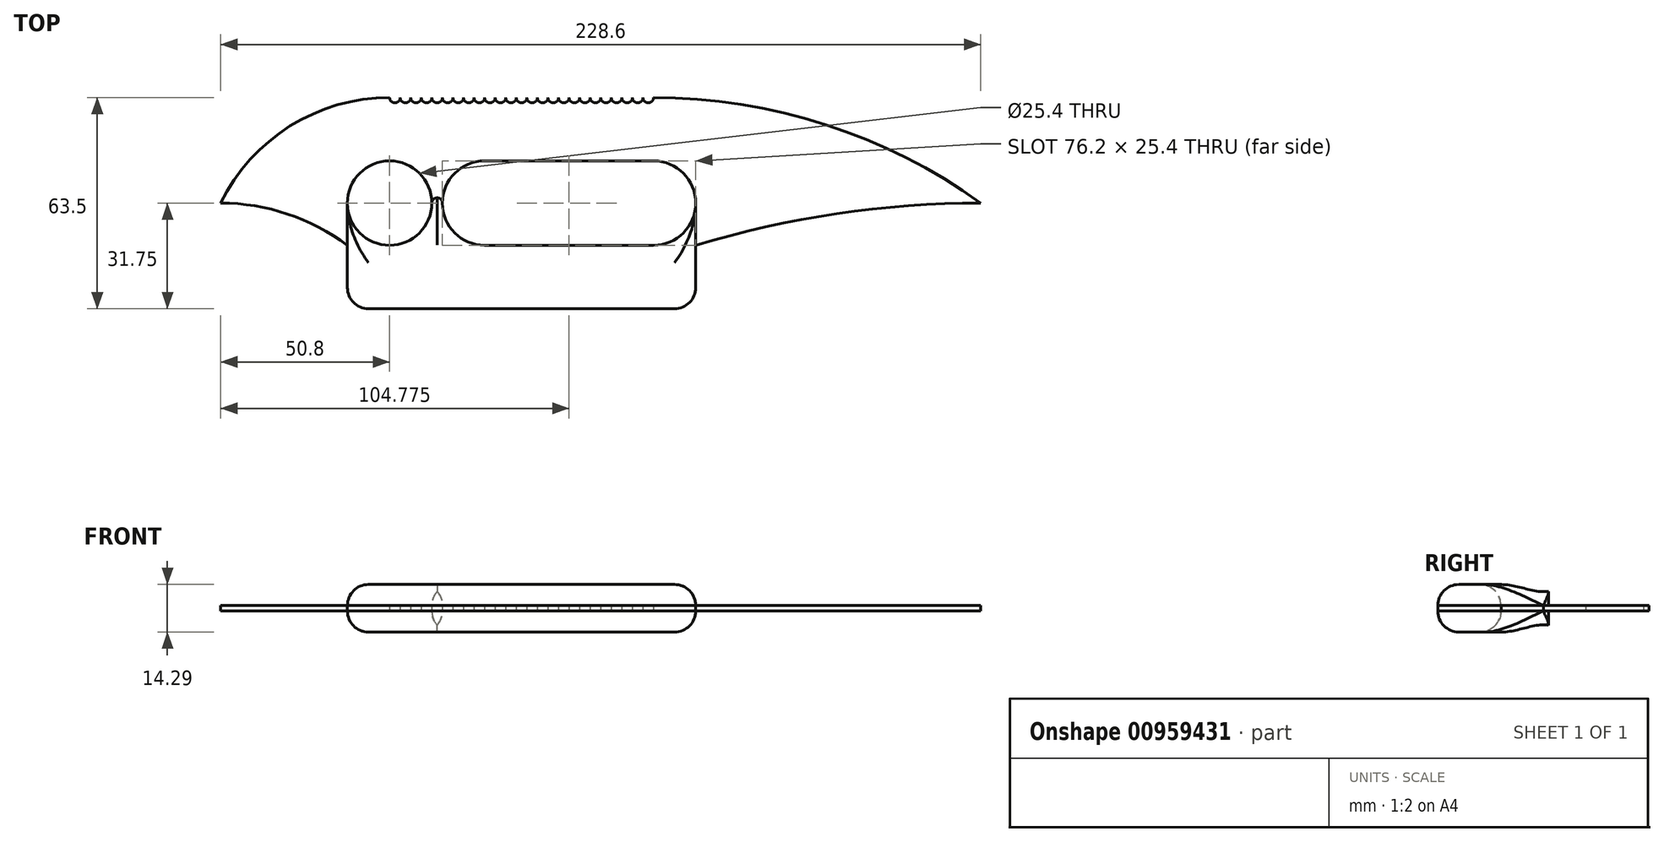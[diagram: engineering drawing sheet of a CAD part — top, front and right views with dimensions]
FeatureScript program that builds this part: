
annotation { "Feature Type Name" : "Feature", "Feature Type Description" : "" }
export const myFeature = defineFeature(function(context is Context, id is Id, definition is map)
    precondition{}
    {
        {
            var Q0;
            Q0=qCreatedBy(makeId("Top.planeOp"),FACE);
            var sketch = newSketch(context, id + "F0", { "sketchPlane" : qUnion([Q0])});
            skCircle(sketch, "E0", {"center": v(0, 0) * mm, "radius": 127 * mm, "construction": true});
            skCircle(sketch, "E1", {"center": v(-63.5, 0) * mm, "radius": 12.7 * mm});
            skArc(sketch, "E2", {"start": v(-34.92, -12.7) * mm, "mid": v(-47.62, 0) * mm, "end": v(-34.92, 12.7) * mm});
            skArc(sketch, "E3", {"start": v(15.88, 12.7) * mm, "mid": v(28.58, 0) * mm, "end": v(15.88, -12.7) * mm});
            skLineSegment(sketch, "E4", {"start": v(-34.92, 12.7) * mm, "end": v(15.88, 12.7) * mm});
            skLineSegment(sketch, "E5", {"start": v(15.88, -12.7) * mm, "end": v(-34.92, -12.7) * mm});
            skPoint(sketch, "E6", {"position": v(-114.3, 0) * mm});
            skPoint(sketch, "E7", {"position": v(114.3, 0) * mm});
            skPoint(sketch, "E8", {"position": v(-76.2, 0) * mm});
            skPoint(sketch, "E9", {"position": v(-63.5, -12.7) * mm});
            skPoint(sketch, "E10.oppositeSnap0", {"position": v(28.58, 0) * mm});
            skLineSegment(sketch, "E10.bottom", {"start": v(-76.2, -12.7) * mm, "end": v(28.58, -12.7) * mm, "construction": true});
            skLineSegment(sketch, "E10.top", {"start": v(-69.85, -31.75) * mm, "end": v(22.23, -31.75) * mm});
            skLineSegment(sketch, "E10.left", {"start": v(-76.2, -12.7) * mm, "end": v(-76.2, -25.4) * mm});
            skLineSegment(sketch, "E10.right", {"start": v(28.58, -12.7) * mm, "end": v(28.58, -25.4) * mm});
            skArc(sketch, "E11", {"start": v(-76.2, -12.7) * mm, "mid": v(-94.22, -3.26) * mm, "end": v(-114.3, 0) * mm});
            skLineSegment(sketch, "E12", {"start": v(-114.3, 0) * mm, "end": v(114.3, 0) * mm, "construction": true});
            skArc(sketch, "E13", {"start": v(114.3, 0) * mm, "mid": v(70.97, -3.2) * mm, "end": v(28.57, -12.7) * mm});
            skArc(sketch, "E14", {"start": v(114.3, 0) * mm, "mid": v(67.58, 23.62) * mm, "end": v(15.88, 31.75) * mm});
            skArc(sketch, "E15", {"start": v(-63.5, 31.75) * mm, "mid": v(-93.45, 23.16) * mm, "end": v(-114.3, 0) * mm});
            skLineSegment(sketch, "E16", {"start": v(-63.5, 31.75) * mm, "end": v(15.88, 31.75) * mm, "construction": true});
            skPoint(sketch, "E17.visualSharp", {"position": v(-76.2, -31.75) * mm});
            skArc(sketch, "E17.filletArc", {"start": v(-76.2, -25.4) * mm, "mid": v(-74.34, -29.9) * mm, "end": v(-69.85, -31.75) * mm});
            skPoint(sketch, "E18.visualSharp", {"position": v(28.58, -31.75) * mm});
            skArc(sketch, "E18.filletArc", {"start": v(22.23, -31.75) * mm, "mid": v(26.72, -29.9) * mm, "end": v(28.58, -25.4) * mm});
            skArc(sketch, "E19", {"start": v(-63.5, 31.75) * mm, "mid": v(-61.91, 30.16) * mm, "end": v(-60.32, 31.75) * mm});
            skArc(sketch, "E20", {"start": v(-60.33, 31.75) * mm, "mid": v(-58.74, 30.16) * mm, "end": v(-57.15, 31.75) * mm});
            skArc(sketch, "E21", {"start": v(-57.15, 31.75) * mm, "mid": v(-55.56, 30.16) * mm, "end": v(-53.98, 31.75) * mm});
            skArc(sketch, "E22", {"start": v(-53.98, 31.75) * mm, "mid": v(-52.39, 30.16) * mm, "end": v(-50.8, 31.75) * mm});
            skArc(sketch, "E23", {"start": v(-50.8, 31.75) * mm, "mid": v(-49.21, 30.16) * mm, "end": v(-47.63, 31.75) * mm});
            skArc(sketch, "E24", {"start": v(-47.63, 31.75) * mm, "mid": v(-46.04, 30.16) * mm, "end": v(-44.45, 31.75) * mm});
            skArc(sketch, "E25", {"start": v(-44.45, 31.75) * mm, "mid": v(-42.86, 30.16) * mm, "end": v(-41.28, 31.75) * mm});
            skArc(sketch, "E26", {"start": v(-41.28, 31.75) * mm, "mid": v(-39.69, 30.16) * mm, "end": v(-38.1, 31.75) * mm});
            skArc(sketch, "E27", {"start": v(-38.1, 31.75) * mm, "mid": v(-36.51, 30.16) * mm, "end": v(-34.93, 31.75) * mm});
            skArc(sketch, "E28", {"start": v(-34.93, 31.75) * mm, "mid": v(-33.34, 30.16) * mm, "end": v(-31.75, 31.75) * mm});
            skArc(sketch, "E29", {"start": v(-31.75, 31.75) * mm, "mid": v(-30.16, 30.16) * mm, "end": v(-28.58, 31.75) * mm});
            skArc(sketch, "E30", {"start": v(-28.58, 31.75) * mm, "mid": v(-26.99, 30.16) * mm, "end": v(-25.4, 31.75) * mm});
            skArc(sketch, "E31", {"start": v(-25.4, 31.75) * mm, "mid": v(-23.81, 30.16) * mm, "end": v(-22.23, 31.75) * mm});
            skArc(sketch, "E32", {"start": v(-22.23, 31.75) * mm, "mid": v(-20.64, 30.16) * mm, "end": v(-19.05, 31.75) * mm});
            skArc(sketch, "E33", {"start": v(-19.05, 31.75) * mm, "mid": v(-17.46, 30.16) * mm, "end": v(-15.88, 31.75) * mm});
            skArc(sketch, "E34", {"start": v(-15.88, 31.75) * mm, "mid": v(-14.29, 30.16) * mm, "end": v(-12.7, 31.75) * mm});
            skArc(sketch, "E35", {"start": v(-12.7, 31.75) * mm, "mid": v(-11.11, 30.16) * mm, "end": v(-9.53, 31.75) * mm});
            skArc(sketch, "E36", {"start": v(-9.53, 31.75) * mm, "mid": v(-7.94, 30.16) * mm, "end": v(-6.35, 31.75) * mm});
            skArc(sketch, "E37", {"start": v(-6.35, 31.75) * mm, "mid": v(-4.76, 30.16) * mm, "end": v(-3.18, 31.75) * mm});
            skArc(sketch, "E38", {"start": v(-3.18, 31.75) * mm, "mid": v(-1.59, 30.16) * mm, "end": v(0, 31.75) * mm});
            skArc(sketch, "E39", {"start": v(0, 31.75) * mm, "mid": v(1.59, 30.16) * mm, "end": v(3.17, 31.75) * mm});
            skArc(sketch, "E40", {"start": v(3.17, 31.75) * mm, "mid": v(4.76, 30.16) * mm, "end": v(6.35, 31.75) * mm});
            skArc(sketch, "E41", {"start": v(6.35, 31.75) * mm, "mid": v(7.94, 30.16) * mm, "end": v(9.52, 31.75) * mm});
            skArc(sketch, "E42", {"start": v(9.52, 31.75) * mm, "mid": v(11.11, 30.16) * mm, "end": v(12.7, 31.75) * mm});
            skArc(sketch, "E43", {"start": v(12.7, 31.75) * mm, "mid": v(14.29, 30.16) * mm, "end": v(15.87, 31.75) * mm});
            skSolve(sketch);
        }
        {
            var Q0;
            Q0 = qSketchRegion(id + "F0", true);
            extrude(context, id + "F1", {"entities" : qUnion([Q0]), "depth" : 1.59 * mm, "offsetDistance" : 25.4 * mm});
        }
        {
            var Q0;
            Q0=makeQuery(id+"F1.opExtrude","CAP_FACE",FACE,{"disambiguationData":[OSD([sQuery(id+"F0.wireOp",EDGE,"E1"),sQuery(id+"F0.wireOp",EDGE,"E2"),sQuery(id+"F0.wireOp",EDGE,"E3"),sQuery(id+"F0.wireOp",EDGE,"E4"),sQuery(id+"F0.wireOp",EDGE,"E5"),sQuery(id+"F0.wireOp",EDGE,"E10.top"),sQuery(id+"F0.wireOp",EDGE,"E10.left"),sQuery(id+"F0.wireOp",EDGE,"E10.right"),sQuery(id+"F0.wireOp",EDGE,"E11"),sQuery(id+"F0.wireOp",EDGE,"E13"),sQuery(id+"F0.wireOp",EDGE,"E14"),sQuery(id+"F0.wireOp",EDGE,"E15"),sQuery(id+"F0.wireOp",EDGE,"E17.filletArc"),sQuery(id+"F0.wireOp",EDGE,"E18.filletArc"),sQuery(id+"F0.wireOp",EDGE,"E19"),sQuery(id+"F0.wireOp",EDGE,"E20"),sQuery(id+"F0.wireOp",EDGE,"E21"),sQuery(id+"F0.wireOp",EDGE,"E22"),sQuery(id+"F0.wireOp",EDGE,"E23"),sQuery(id+"F0.wireOp",EDGE,"E24"),sQuery(id+"F0.wireOp",EDGE,"E25"),sQuery(id+"F0.wireOp",EDGE,"E26"),sQuery(id+"F0.wireOp",EDGE,"E27"),sQuery(id+"F0.wireOp",EDGE,"E28"),sQuery(id+"F0.wireOp",EDGE,"E29"),sQuery(id+"F0.wireOp",EDGE,"E30"),sQuery(id+"F0.wireOp",EDGE,"E31"),sQuery(id+"F0.wireOp",EDGE,"E32"),sQuery(id+"F0.wireOp",EDGE,"E33"),sQuery(id+"F0.wireOp",EDGE,"E34"),sQuery(id+"F0.wireOp",EDGE,"E35"),sQuery(id+"F0.wireOp",EDGE,"E36"),sQuery(id+"F0.wireOp",EDGE,"E37"),sQuery(id+"F0.wireOp",EDGE,"E38"),sQuery(id+"F0.wireOp",EDGE,"E39"),sQuery(id+"F0.wireOp",EDGE,"E40"),sQuery(id+"F0.wireOp",EDGE,"E41"),sQuery(id+"F0.wireOp",EDGE,"E42"),sQuery(id+"F0.wireOp",EDGE,"E43")])],"isStart":false});
            var sketch = newSketch(context, id + "F2", { "sketchPlane" : qUnion([Q0])});
            skLineSegment(sketch, "E44", {"start": v(-76.2, -12.7) * mm, "end": v(-76.2, 0) * mm});
            skLineSegment(sketch, "E45", {"start": v(28.58, -12.7) * mm, "end": v(28.58, 0) * mm});
            skArc(sketch, "E46", {"start": v(-47.62, 0) * mm, "mid": v(-49.21, 1.59) * mm, "end": v(-50.8, 0) * mm});
            skPoint(sketch, "E46.endSnap0", {"position": v(-47.62, 0) * mm});
            skSolve(sketch);
        }
        {
            var Q0;
            {var subQ3=sQuery(id+"F2.wireOp",EDGE,"E44");Q0=makeQuery(id+"F2.imprint","IMPRINT",FACE,{"disambiguationData":[TD([[makeQuery(id+"F2.imprint","IMPRINT",EDGE,{"derivedFrom":subQ3}),-1.0]])]});}
            extrude(context, id + "F3", {"entities" : qUnion([Q0]), "depth" : 6.35 * mm, "offsetDistance" : 25.4 * mm});
        }
        {
            var Q0;
            Q0=makeQuery(id+"F1.opExtrude","CAP_FACE",FACE,{"disambiguationData":[OSD([sQuery(id+"F0.wireOp",EDGE,"E1"),sQuery(id+"F0.wireOp",EDGE,"E2"),sQuery(id+"F0.wireOp",EDGE,"E3"),sQuery(id+"F0.wireOp",EDGE,"E4"),sQuery(id+"F0.wireOp",EDGE,"E5"),sQuery(id+"F0.wireOp",EDGE,"E10.top"),sQuery(id+"F0.wireOp",EDGE,"E10.left"),sQuery(id+"F0.wireOp",EDGE,"E10.right"),sQuery(id+"F0.wireOp",EDGE,"E11"),sQuery(id+"F0.wireOp",EDGE,"E13"),sQuery(id+"F0.wireOp",EDGE,"E14"),sQuery(id+"F0.wireOp",EDGE,"E15"),sQuery(id+"F0.wireOp",EDGE,"E17.filletArc"),sQuery(id+"F0.wireOp",EDGE,"E18.filletArc"),sQuery(id+"F0.wireOp",EDGE,"E19"),sQuery(id+"F0.wireOp",EDGE,"E20"),sQuery(id+"F0.wireOp",EDGE,"E21"),sQuery(id+"F0.wireOp",EDGE,"E22"),sQuery(id+"F0.wireOp",EDGE,"E23"),sQuery(id+"F0.wireOp",EDGE,"E24"),sQuery(id+"F0.wireOp",EDGE,"E25"),sQuery(id+"F0.wireOp",EDGE,"E26"),sQuery(id+"F0.wireOp",EDGE,"E27"),sQuery(id+"F0.wireOp",EDGE,"E28"),sQuery(id+"F0.wireOp",EDGE,"E29"),sQuery(id+"F0.wireOp",EDGE,"E30"),sQuery(id+"F0.wireOp",EDGE,"E31"),sQuery(id+"F0.wireOp",EDGE,"E32"),sQuery(id+"F0.wireOp",EDGE,"E33"),sQuery(id+"F0.wireOp",EDGE,"E34"),sQuery(id+"F0.wireOp",EDGE,"E35"),sQuery(id+"F0.wireOp",EDGE,"E36"),sQuery(id+"F0.wireOp",EDGE,"E37"),sQuery(id+"F0.wireOp",EDGE,"E38"),sQuery(id+"F0.wireOp",EDGE,"E39"),sQuery(id+"F0.wireOp",EDGE,"E40"),sQuery(id+"F0.wireOp",EDGE,"E41"),sQuery(id+"F0.wireOp",EDGE,"E42"),sQuery(id+"F0.wireOp",EDGE,"E43")])],"isStart":true});
            var sketch = newSketch(context, id + "F4", { "sketchPlane" : qUnion([Q0])});
            skLineSegment(sketch, "E47", {"start": v(28.58, 12.7) * mm, "end": v(28.58, 0) * mm});
            skLineSegment(sketch, "E48", {"start": v(-76.2, 12.7) * mm, "end": v(-76.2, 0) * mm});
            skArc(sketch, "E49", {"start": v(-50.8, 0) * mm, "mid": v(-49.21, -1.59) * mm, "end": v(-47.62, 0) * mm});
            skSolve(sketch);
        }
        {
            var Q0;
            {var subQ3=sQuery(id+"F4.wireOp",EDGE,"E47");Q0=makeQuery(id+"F4.imprint","IMPRINT",FACE,{"disambiguationData":[TD([[makeQuery(id+"F4.imprint","IMPRINT",EDGE,{"derivedFrom":subQ3}),-1.0]])]});}
            extrude(context, id + "F5", {"entities" : qUnion([Q0]), "depth" : 6.35 * mm, "offsetDistance" : 25.4 * mm});
        }
        {
            var Q0;
            Q0=makeQuery(id+"F3.opExtrude","CAP_EDGE",EDGE,{"disambiguationData":[OSD([sQuery(id+"F0.wireOp",EDGE,"E10.top")])],"isStart":false});
            var Q1;
            Q1=makeQuery(id+"F5.opExtrude","CAP_EDGE",EDGE,{"disambiguationData":[OSD([sQuery(id+"F0.wireOp",EDGE,"E10.top")])],"isStart":false});
            var Q2;
            Q2=makeQuery(id+"F3.opExtrude","CAP_EDGE",EDGE,{"disambiguationData":[OSD([sQuery(id+"F0.wireOp",EDGE,"E10.left"),sQuery(id+"F2.wireOp",EDGE,"E44")])],"isStart":false});
            var Q3;
            Q3=makeQuery(id+"F5.opExtrude","CAP_EDGE",EDGE,{"disambiguationData":[OSD([sQuery(id+"F0.wireOp",EDGE,"E10.left"),sQuery(id+"F4.wireOp",EDGE,"E48")])],"isStart":false});
            var Q4;
            Q4=makeQuery(id+"F3.opExtrude","CAP_EDGE",EDGE,{"disambiguationData":[OSD([sQuery(id+"F0.wireOp",EDGE,"E10.right"),sQuery(id+"F2.wireOp",EDGE,"E45")])],"isStart":false});
            var Q5;
            Q5=makeQuery(id+"F5.opExtrude","CAP_EDGE",EDGE,{"disambiguationData":[OSD([sQuery(id+"F0.wireOp",EDGE,"E10.right"),sQuery(id+"F4.wireOp",EDGE,"E47")])],"isStart":false});
            var Q6;
            Q6=makeQuery(id+"F3.opExtrude","CAP_EDGE",EDGE,{"disambiguationData":[OSD([sQuery(id+"F0.wireOp",EDGE,"E1")])],"isStart":false});
            var Q7;
            Q7=makeQuery(id+"F3.opExtrude","CAP_EDGE",EDGE,{"disambiguationData":[OSD([sQuery(id+"F0.wireOp",EDGE,"E5")])],"isStart":false});
            var Q8;
            Q8=makeQuery(id+"F5.opExtrude","CAP_EDGE",EDGE,{"disambiguationData":[OSD([sQuery(id+"F0.wireOp",EDGE,"E5")])],"isStart":false});
            var Q9;
            Q9=makeQuery(id+"F5.opExtrude","CAP_EDGE",EDGE,{"disambiguationData":[OSD([sQuery(id+"F0.wireOp",EDGE,"E1")])],"isStart":false});
            fillet(context, id + "F6", {"entities" : qUnion([Q0, Q1, Q2, Q3, Q4, Q5, Q6, Q7, Q8, Q9]), "radius" : 6.35 * mm, "allowEdgeOverflow" : false});
        }
    });
